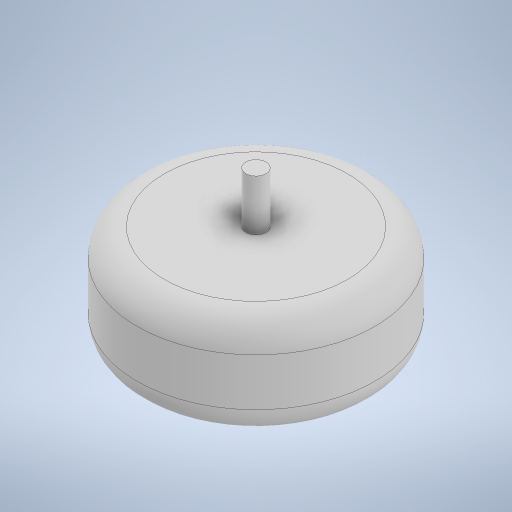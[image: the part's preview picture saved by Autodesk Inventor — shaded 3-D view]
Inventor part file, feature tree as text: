
AUTODESK INVENTOR PART (.ipt)
format: ipt  version: 2024 (Build 280153000, 153)  size: 250,368 bytes
history: native  units: mm
features: extrude x2, sketch x2, fillet x1
ambient origin geometry x8: Origin, YZ Plane, XZ Plane, XY Plane, X Axis, Y Axis, Z Axis, Center Point
bodies: Solid1 (feature_tree)
feature tree (5):
  extrude  "Extrusion1"  Depth=30.0mm TaperAngle=0.0deg
  extrude  "Extrusion2"  Depth=16.0mm
  fillet  "Fillet1"  Radius=16.0mm
  sketch  "Sketch1"  dims[d0=60.0mm d1=0.0mm d2=30.0mm d3=0.0mm]
  sketch  "Sketch2"  dims[d4=140.0mm d5=12.0mm d6=16.0mm]
